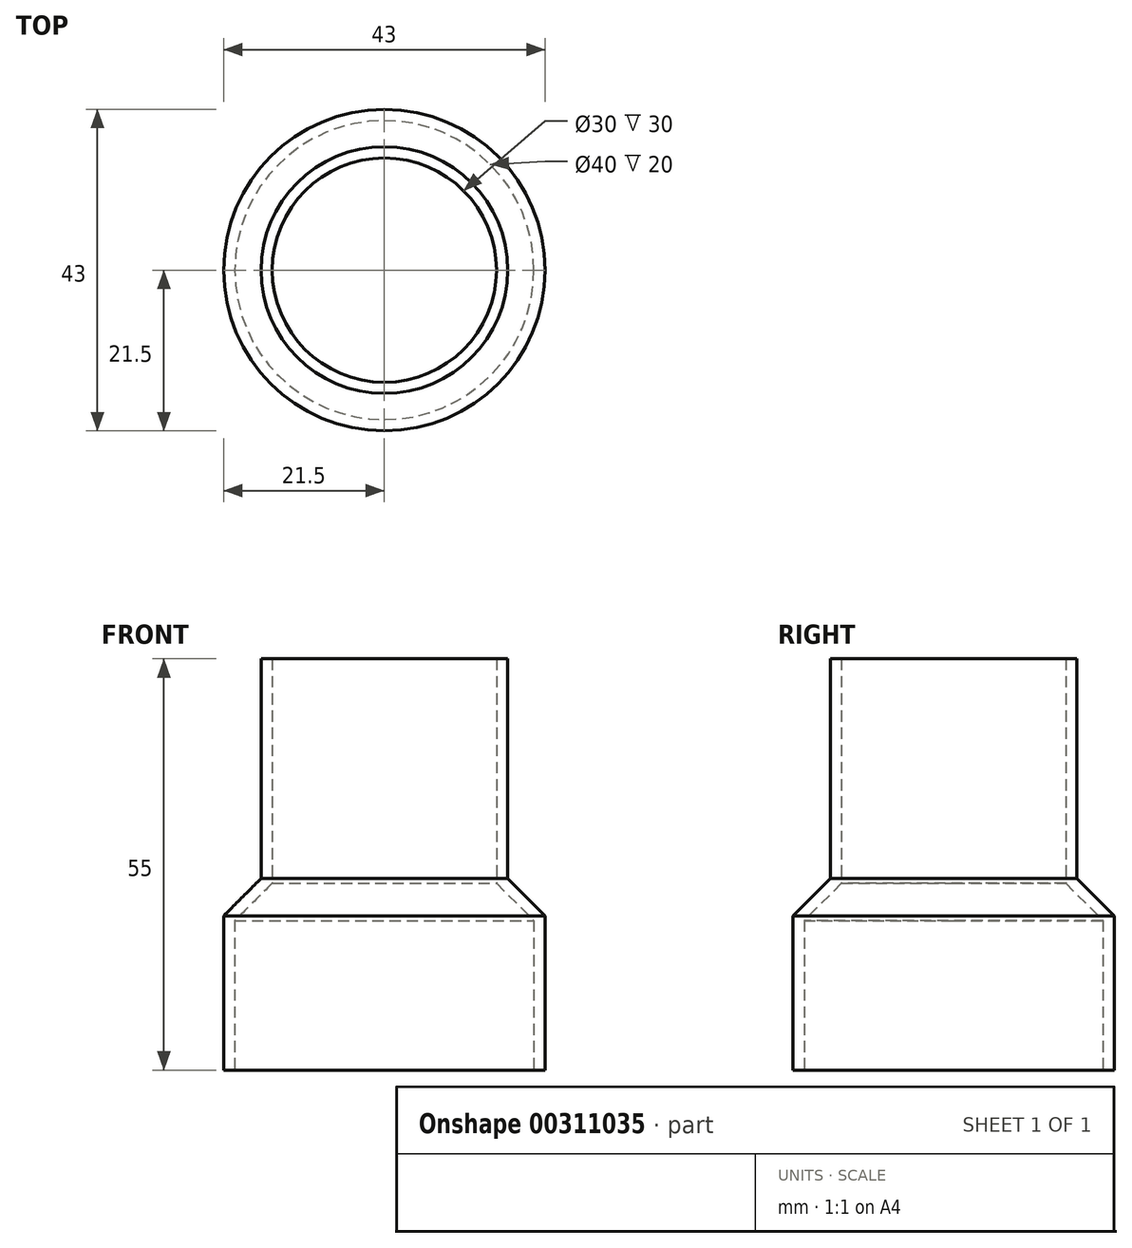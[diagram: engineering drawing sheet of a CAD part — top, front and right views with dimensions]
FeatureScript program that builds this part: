
annotation { "Feature Type Name" : "Feature", "Feature Type Description" : "" }
export const myFeature = defineFeature(function(context is Context, id is Id, definition is map)
    precondition{}
    {
        {
            var Q0;
            Q0=qCreatedBy(makeId("Front.planeOp"),FACE);
            var sketch = newSketch(context, id + "F0", { "sketchPlane" : qUnion([Q0])});
            skLineSegment(sketch, "E0", {"start": v(15, 55) * mm, "end": v(15, 25) * mm});
            skLineSegment(sketch, "E1", {"start": v(15, 25) * mm, "end": v(20, 20) * mm});
            skLineSegment(sketch, "E2", {"start": v(20, 20) * mm, "end": v(20, 0) * mm});
            skLineSegment(sketch, "E3", {"start": v(0, 0) * mm, "end": v(0, 51.25) * mm, "construction": true});
            skLineSegment(sketch, "E4", {"start": v(15, 55) * mm, "end": v(16.5, 55) * mm});
            skLineSegment(sketch, "E5", {"start": v(16.5, 55) * mm, "end": v(16.5, 25.62) * mm});
            skLineSegment(sketch, "E6", {"start": v(16.5, 25.62) * mm, "end": v(21.5, 20.62) * mm});
            skLineSegment(sketch, "E7", {"start": v(21.5, 20.62) * mm, "end": v(21.5, 0) * mm});
            skLineSegment(sketch, "E8", {"start": v(21.5, 0) * mm, "end": v(20, 0) * mm});
            skSolve(sketch);
        }
        {
            var Q0;
            Q0 = qSketchRegion(id + "F0", true);
            var Q1;
            Q1=sQuery(id+"F0.wireOp",EDGE,"E3");
            revolve(context, id + "F1", {"entities" : qUnion([Q0]), "axis" : qUnion([Q1]), "revolveType" : RevolveType.FULL});
        }
    });
